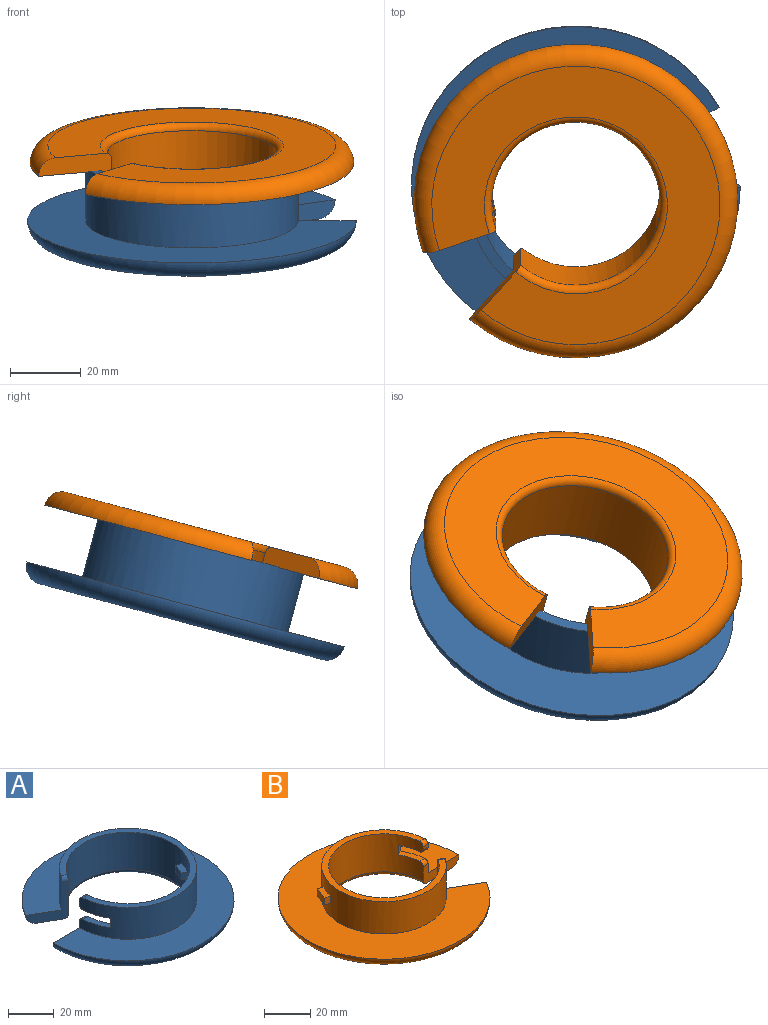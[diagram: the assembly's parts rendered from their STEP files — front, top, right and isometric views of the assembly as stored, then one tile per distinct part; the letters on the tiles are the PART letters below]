
ASSEMBLY  parts=2 mates=1
PART A: 22 faces, bbox 100.3x100.3x22 mm
  f0: cylinder r=30mm len=60mm, axis (0,0,-1), area 2855.4mm2, adj f2,f3,f4,f8,f9,f15,f16,f17
  f1: cylinder r=27mm len=54mm, axis (0,0,-1), area 3010.6mm2, adj f2,f3,f7,f8,f9,f10,f11,f12
  f2: plane 19.33x8.5mm, normal (0,1,0), area 100.9mm2, adj f0,f1,f4,f5,f6,f7,f18
  f3: plane 60x59.93mm, normal (0,0,1), area 480.4mm2, adj f0,f1,f20,f21
  f4: plane 92.66x92.66mm, normal (0,0,1), area 3589mm2, adj f0,f2,f5,f8
  f5: torus R=41.33mm, axis (0,0,-1), area 2013.5mm2, adj f2,f4,f6,f8
  f6: plane 82.66x82.66mm, normal (0,0,-1), area 2496.8mm2, adj f2,f5,f7,f8
  f7: torus R=29mm, axis (0,0,-1), area 501.7mm2, adj f1,f2,f6,f8
  f8: plane 20x16.74mm, normal (-0.5,-0.87,0), area 135.4mm2, adj f0,f1,f4,f5,f6,f7,f21
  f9: plane 3x2.5mm, normal (0,1,0), area 7.5mm2, adj f0,f1,f19,f20
  f10: plane 3.6x2.6mm, normal (-0.5,-0.87,0), area 10.8mm2, adj f1,f12,f13,f14
  f11: plane 3.6x2.9mm, normal (0.26,0.97,0), area 10.8mm2, adj f1,f12,f13,f14
  f12: plane 7.29x5.3mm, normal (0,0,1), area 20mm2, adj f1,f10,f11,f14
  f13: plane 7.29x5.3mm, normal (0,0,-1), area 20mm2, adj f1,f10,f11,f14
  f14: cylinder r=24mm len=5.79mm, axis (0,0,-1), area 22.6mm2, adj f10,f11,f12,f13
  f15: plane 5x2.6mm, normal (-0.5,0.87,0), area 15mm2, adj f0,f1,f16,f17
  f16: plane 13x6.55mm, normal (0,0,1), area 38.8mm2, adj f0,f1,f15,f18
  f17: plane 13x6.55mm, normal (0,0,-1), area 38.8mm2, adj f0,f1,f15,f19
  f18: cylinder r=2mm len=3.07mm, axis (1,0,0), area 9.4mm2, adj f0,f1,f2,f16
  f19: cylinder r=2mm len=3.07mm, axis (-1,0,0), area 9.4mm2, adj f0,f1,f9,f17
  f20: cylinder r=2mm len=3.07mm, axis (-1,0,0), area 9.4mm2, adj f0,f1,f3,f9
  f21: cylinder r=2mm len=3.66mm, axis (0.87,-0.5,0), area 9.4mm2, adj f0,f1,f3,f8
PART B: 22 faces, bbox 98.8x98.8x22 mm
  f0: cylinder r=23.8mm len=47.6mm, axis (0,0,-1), area 2675.8mm2, adj f2,f3,f4,f8,f9,f10,f11,f12
  f1: cylinder r=26.8mm len=53.6mm, axis (0,0,-1), area 2525.2mm2, adj f2,f4,f5,f8,f9,f10,f11,f12
  f2: plane 21.83x9.5mm, normal (0,-1,0), area 116.4mm2, adj f0,f1,f3,f5,f6,f7,f14
  f3: torus R=25.8mm, axis (0,0,-1), area 443.8mm2, adj f0,f2,f7,f8
  f4: plane 53.6x53.53mm, normal (0,0,1), area 425.1mm2, adj f0,f1,f15,f16
  f5: plane 91.26x91.26mm, normal (0,0,1), area 3927.1mm2, adj f1,f2,f6,f8
  f6: torus R=40.63mm, axis (0,0,-1), area 1981.8mm2, adj f2,f5,f7,f8
  f7: plane 81.26x81.26mm, normal (0,0,-1), area 2836.6mm2, adj f2,f3,f6,f8
  f8: plane 20x18.9mm, normal (0.5,0.87,0), area 147.9mm2, adj f0,f1,f3,f5,f6,f7,f16
  f9: plane 3x1.5mm, normal (0,-1,0), area 4.5mm2, adj f0,f1,f13,f15
  f10: plane 5x2.6mm, normal (0.5,-0.87,0), area 15mm2, adj f0,f1,f11,f12
  f11: plane 11.4x6.11mm, normal (0,0,1), area 33.7mm2, adj f0,f1,f10,f14
  f12: plane 11.4x6.11mm, normal (0,0,-1), area 33.7mm2, adj f0,f1,f10,f13
  f13: cylinder r=2mm len=3.08mm, axis (1,0,0), area 9.4mm2, adj f0,f1,f9,f12
  f14: cylinder r=2mm len=3.08mm, axis (-1,0,0), area 9.4mm2, adj f0,f1,f2,f11
  f15: cylinder r=2mm len=3.08mm, axis (1,0,0), area 9.4mm2, adj f0,f1,f4,f9
  f16: cylinder r=2mm len=3.67mm, axis (-0.87,0.5,0), area 9.4mm2, adj f0,f1,f4,f8
  f17: plane 3.6x2.62mm, normal (0.49,0.87,0), area 10.8mm2, adj f1,f19,f20,f21
  f18: plane 3.6x2.91mm, normal (-0.25,-0.97,0), area 10.8mm2, adj f1,f19,f20,f21
  f19: cylinder r=29.8mm len=7.23mm, axis (0,0,-1), area 28.1mm2, adj f17,f18,f20,f21
  f20: plane 7.96x5.49mm, normal (0,0,1), area 22.2mm2, adj f1,f17,f18,f19
  f21: plane 7.96x5.49mm, normal (0,0,-1), area 22.2mm2, adj f1,f17,f18,f19
PLACE A rot(axis=(0.03,0.13,-0.99),150.8deg) t=(224.43,-160.92,-49.78)mm
PLACE B rot(axis=(-0.16,0.98,0.13),177.6deg) t=(224.43,-165.27,-33.54)mm
MATE cylindrical B.f0 <-> A.f0  axis (0,0.26,-0.97) through (224.43,-165.27,-33.54)mm
